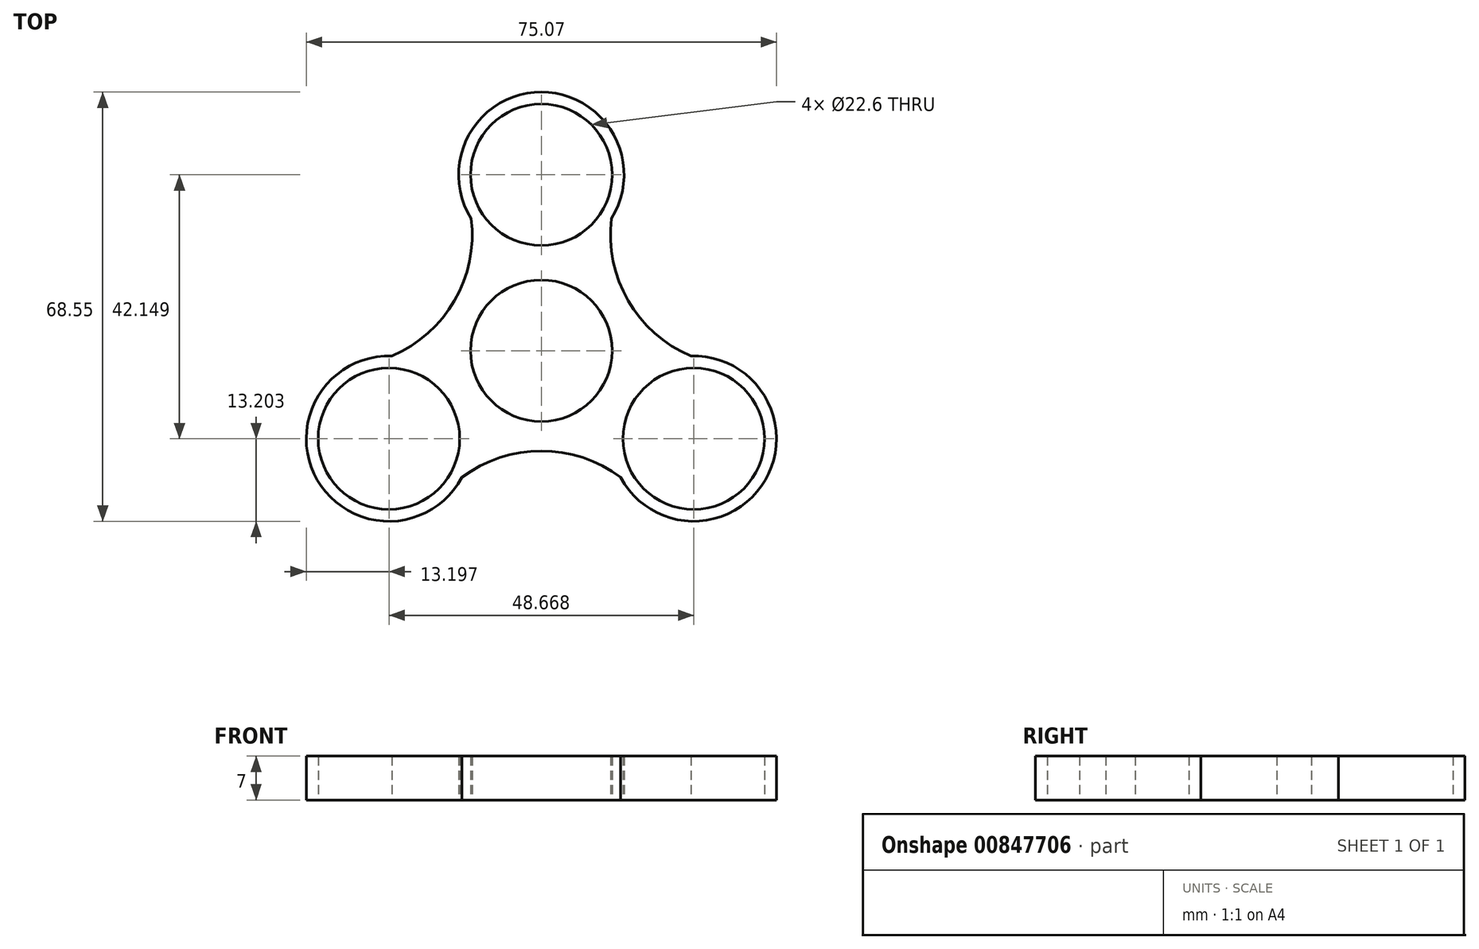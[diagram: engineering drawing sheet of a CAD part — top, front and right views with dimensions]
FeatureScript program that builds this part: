
annotation { "Feature Type Name" : "Feature", "Feature Type Description" : "" }
export const myFeature = defineFeature(function(context is Context, id is Id, definition is map)
    precondition{}
    {
        {
            var Q0;
            Q0=qCreatedBy(makeId("Top.planeOp"),FACE);
            var sketch = newSketch(context, id + "F0", { "sketchPlane" : qUnion([Q0])});
            skCircle(sketch, "E0", {"center": v(0, 0) * mm, "radius": 11.3 * mm});
            skCircle(sketch, "E1", {"center": v(0, 28.1) * mm, "radius": 11.3 * mm});
            skArc(sketch, "E2", {"start": v(11.2, 21.1) * mm, "mid": v(0, 41.3) * mm, "end": v(-11.2, 21.1) * mm});
            skCircle(sketch, "E3.1.0", {"center": v(-24.33, -14.05) * mm, "radius": 11.3 * mm});
            skArc(sketch, "E3.1.1", {"start": v(-23.87, -0.86) * mm, "mid": v(-35.76, -20.65) * mm, "end": v(-12.67, -20.24) * mm});
            skCircle(sketch, "E3.2.0", {"center": v(24.34, -14.05) * mm, "radius": 11.3 * mm});
            skArc(sketch, "E3.2.1", {"start": v(12.68, -20.24) * mm, "mid": v(35.77, -20.64) * mm, "end": v(23.87, -0.85) * mm});
            skArc(sketch, "E4", {"start": v(12.68, -20.24) * mm, "mid": v(0, -16) * mm, "end": v(-12.67, -20.24) * mm});
            skArc(sketch, "E5.1.0", {"start": v(11.2, 21.1) * mm, "mid": v(13.86, 8) * mm, "end": v(23.87, -0.85) * mm});
            skArc(sketch, "E5.2.0", {"start": v(-23.87, -0.86) * mm, "mid": v(-13.86, 8) * mm, "end": v(-11.2, 21.1) * mm});
            skSolve(sketch);
        }
        {
            var Q0;
            Q0=makeQuery(id+"F0.imprint","IMPRINT",FACE,{"disambiguationData":[TD([[makeQuery(id+"F0.imprint","IMPRINT",EDGE,{"derivedFrom":sQuery(id+"F0.wireOp",EDGE,"E0")}),-1.0]])]});
            extrude(context, id + "F1", {"entities" : qUnion([Q0]), "depth" : 7 * mm, "offsetDistance" : 25 * mm});
        }
    });
